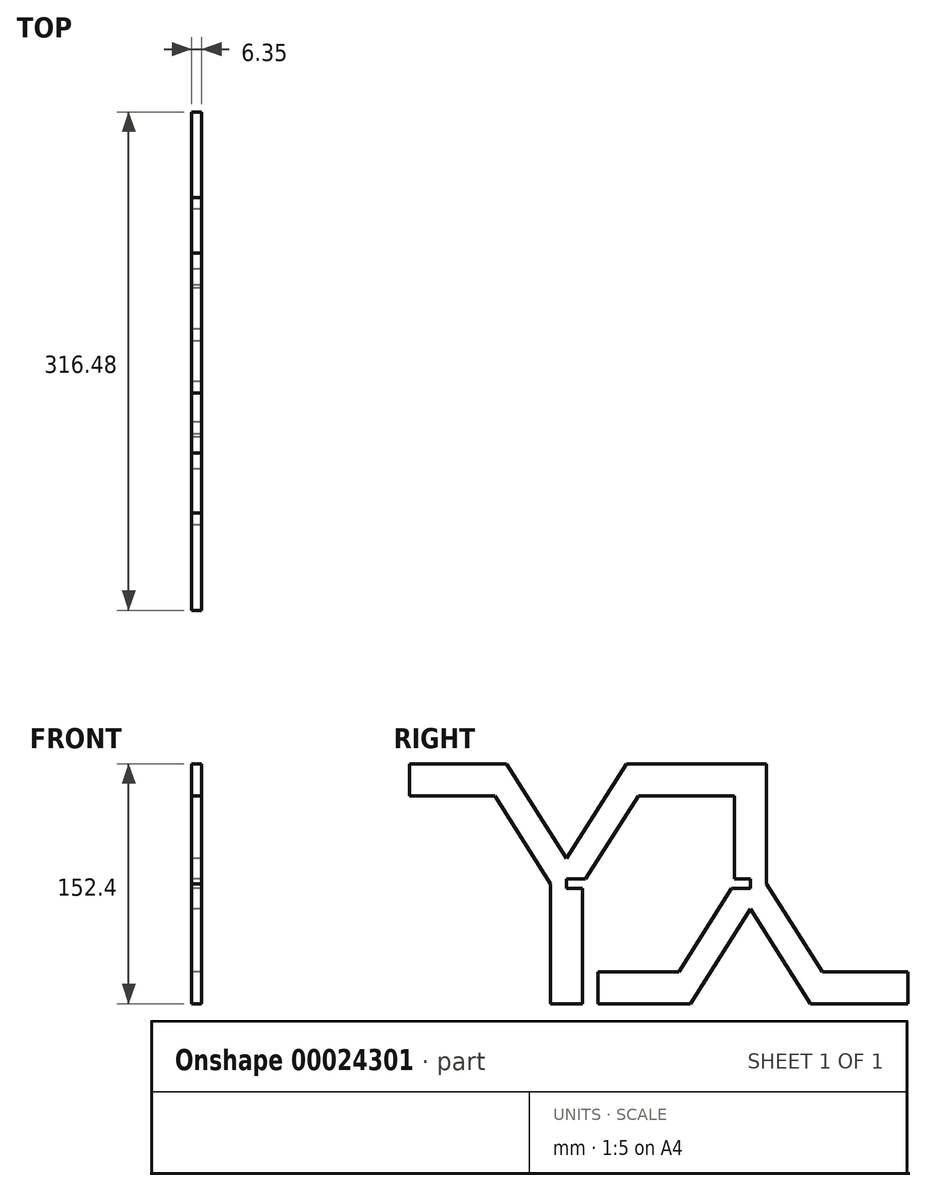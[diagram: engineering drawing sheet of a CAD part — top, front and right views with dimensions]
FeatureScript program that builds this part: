
annotation { "Feature Type Name" : "Feature", "Feature Type Description" : "" }
export const myFeature = defineFeature(function(context is Context, id is Id, definition is map)
    precondition{}
    {
        {
            var Q0;
            Q0=qCreatedBy(makeId("Right.planeOp"),FACE);
            var sketch = newSketch(context, id + "F0", { "sketchPlane" : qUnion([Q0])});
            skLineSegment(sketch, "E0", {"start": v(10.16, 79.25) * mm, "end": v(10.16, 73.15) * mm});
            skLineSegment(sketch, "E1", {"start": v(0, 73.03) * mm, "end": v(0, 0) * mm});
            skLineSegment(sketch, "E2", {"start": v(0, 0) * mm, "end": v(20.32, 0) * mm});
            skLineSegment(sketch, "E3", {"start": v(20.32, 0) * mm, "end": v(20.32, 73.15) * mm});
            skLineSegment(sketch, "E4", {"start": v(22.25, 79.25) * mm, "end": v(55.71, 132.08) * mm});
            skLineSegment(sketch, "E5", {"start": v(68.58, 152.4) * mm, "end": v(48.26, 152.4) * mm});
            skLineSegment(sketch, "E6", {"start": v(48.26, 152.4) * mm, "end": v(10.16, 92.24) * mm});
            skLineSegment(sketch, "E7", {"start": v(10.16, 92.24) * mm, "end": v(-27.94, 152.4) * mm});
            skLineSegment(sketch, "E8", {"start": v(-27.94, 152.4) * mm, "end": v(-48.26, 152.4) * mm});
            skLineSegment(sketch, "E9", {"start": v(-35.4, 132.08) * mm, "end": v(-2.01, 79.38) * mm});
            skLineSegment(sketch, "E10", {"start": v(10.16, 79.25) * mm, "end": v(10.16, 0) * mm, "construction": true});
            skLineSegment(sketch, "E11", {"start": v(10.16, 76.2) * mm, "end": v(0, 76.2) * mm, "construction": true});
            skLineSegment(sketch, "E12", {"start": v(10.16, 76.2) * mm, "end": v(20.32, 76.2) * mm, "construction": true});
            skLineSegment(sketch, "E13", {"start": v(10.16, 79.25) * mm, "end": v(10.16, 152.4) * mm, "construction": true});
            skLineSegment(sketch, "E14", {"start": v(-27.94, 152.4) * mm, "end": v(48.26, 152.4) * mm, "construction": true});
            skLineSegment(sketch, "E15", {"start": v(68.58, 152.4) * mm, "end": v(68.58, 0) * mm, "construction": true});
            skLineSegment(sketch, "E16.1.0", {"start": v(127, 73.15) * mm, "end": v(127, 0.13) * mm, "construction": true});
            skLineSegment(sketch, "E16.1.2", {"start": v(127, 73.15) * mm, "end": v(168.28, 73.15) * mm, "construction": true});
            skLineSegment(sketch, "E16.1.3", {"start": v(172.55, 20.32) * mm, "end": v(137.16, 76.2) * mm});
            skLineSegment(sketch, "E16.1.4", {"start": v(137.16, 81.08) * mm, "end": v(137.16, 152.4) * mm});
            skLineSegment(sketch, "E16.1.5", {"start": v(116.84, 132.08) * mm, "end": v(116.84, 79.25) * mm});
            skLineSegment(sketch, "E16.1.6", {"start": v(114.9, 73.15) * mm, "end": v(81.45, 20.32) * mm});
            skLineSegment(sketch, "E16.1.7", {"start": v(68.58, 0) * mm, "end": v(88.9, 0) * mm});
            skLineSegment(sketch, "E16.1.8", {"start": v(88.9, 0) * mm, "end": v(127, 60.16) * mm});
            skLineSegment(sketch, "E16.1.9", {"start": v(127, 60.16) * mm, "end": v(165.1, 0) * mm});
            skLineSegment(sketch, "E16.1.10", {"start": v(165.1, 0) * mm, "end": v(88.9, 0) * mm, "construction": true});
            skLineSegment(sketch, "E16.1.11", {"start": v(165.1, 0) * mm, "end": v(185.42, 0) * mm});
            skLineSegment(sketch, "E16.1.12", {"start": v(137.16, 152.4) * mm, "end": v(116.84, 152.4) * mm});
            skLineSegment(sketch, "E16.1.15", {"start": v(127, 76.2) * mm, "end": v(137.16, 76.2) * mm, "construction": true});
            skLineSegment(sketch, "E16.1.16", {"start": v(127, 76.2) * mm, "end": v(116.84, 76.2) * mm, "construction": true});
            skPoint(sketch, "E16.center", {"position": v(68.58, 76.2) * mm});
            skLineSegment(sketch, "E16.anchor1", {"start": v(68.58, 76.2) * mm, "end": v(10.16, 79.25) * mm, "construction": true});
            skLineSegment(sketch, "E16.anchor2", {"start": v(68.58, 76.2) * mm, "end": v(127, 73.15) * mm, "construction": true});
            skPoint(sketch, "E17.orphan", {"position": v(127, 79.25) * mm});
            skLineSegment(sketch, "E18", {"start": v(127, 79.25) * mm, "end": v(116.84, 79.25) * mm});
            skLineSegment(sketch, "E19", {"start": v(127, 79.25) * mm, "end": v(127, 73.15) * mm});
            skLineSegment(sketch, "E20", {"start": v(127, 73.15) * mm, "end": v(114.9, 73.15) * mm});
            skLineSegment(sketch, "E21", {"start": v(68.58, 152.4) * mm, "end": v(116.84, 152.4) * mm});
            skLineSegment(sketch, "E22", {"start": v(116.84, 132.08) * mm, "end": v(55.71, 132.08) * mm});
            skLineSegment(sketch, "E23", {"start": v(68.58, 0) * mm, "end": v(29.97, 0) * mm});
            skLineSegment(sketch, "E24", {"start": v(29.97, 0) * mm, "end": v(29.97, 20.32) * mm});
            skLineSegment(sketch, "E25", {"start": v(29.97, 20.32) * mm, "end": v(81.45, 20.32) * mm});
            skLineSegment(sketch, "E26", {"start": v(10.16, 79.25) * mm, "end": v(22.25, 79.25) * mm});
            skLineSegment(sketch, "E27", {"start": v(10.16, 73.15) * mm, "end": v(20.32, 73.15) * mm});
            skLineSegment(sketch, "E28", {"start": v(-2.01, 79.38) * mm, "end": v(0, 76.2) * mm});
            skLineSegment(sketch, "E29", {"start": v(0, 76.2) * mm, "end": v(0, 73.03) * mm});
            skLineSegment(sketch, "E30", {"start": v(137.16, 81.08) * mm, "end": v(137.16, 76.2) * mm});
            skLineSegment(sketch, "E31", {"start": v(-48.26, 152.4) * mm, "end": v(-89.66, 152.4) * mm});
            skLineSegment(sketch, "E32", {"start": v(-89.66, 152.4) * mm, "end": v(-89.66, 132.08) * mm});
            skLineSegment(sketch, "E33", {"start": v(-89.66, 132.08) * mm, "end": v(-35.4, 132.08) * mm});
            skLineSegment(sketch, "E34", {"start": v(185.42, 0) * mm, "end": v(226.82, 0) * mm});
            skLineSegment(sketch, "E35", {"start": v(226.82, 0) * mm, "end": v(226.82, 20.32) * mm});
            skLineSegment(sketch, "E36", {"start": v(226.82, 20.32) * mm, "end": v(172.55, 20.32) * mm});
            skSolve(sketch);
        }
        {
            var Q0;
            Q0 = qSketchRegion(id + "F0", true);
            extrude(context, id + "F1", {"entities" : qUnion([Q0]), "depth" : 6.35 * mm});
        }
    });
